# Revit family: Rotor XLR Series - IXLRADJ
name_source: partatom
category: Acessórios do tubo
units: mm (PartAtom-declared; Revit-internal decimal feet)

## family parameters
Com base no plano de trabalho = Não
Compartilhado = Não
Corte com vazios quando carregada = Não
Cota do conector redondo = Utilizar diâmetro
Número OmniClass = 23.60.30.11.14
Sempre na vertical = Sim
Tipo de parte = Normal
Título OmniClass = Pipework Fittings

## types (9) — shared parameters
Black Plastic = Black Plastic
Blue = Blue Plastic
Cobre = Cobre
DD4 = 1 '
Descrição = IXLRADJ Rotor
Fabricante = Rain Bird
Gray Plastic = Gray Plastic
Modelo = IXLRADJ
RainBird: Code = IXLRADJ
RainBird: Description = IXLRADJ Rotor
RainBird: Product Link = https://www.rainbird.com
Side inlet = Não
SupportProjetos: Level of Detail = LOD 300
SupportProjetos: Reviw = R00
TABLE 100 = TABLE 100psi
TABLE 110 = TABLE 110psi
TABLE 120 = TABLE 120psi
TABLE 30 = TABLE 30psi
TABLE 40 = TABLE 40psi
TABLE 50 = TABLE 50psi
TABLE 60 = TABLE 60psi
TABLE 70 = TABLE 70psi
TABLE 80 = TABLE 80psi
TABLE 90 = TABLE 90psi
URL = https://www.rainbird.com
Water = Water
zero-valued in all types: Body height, Conection, DD, DD1, DD10, DD11, DD12, DD13, DD3, DD5, DD7, Elevação padrão, H1, Pop up height, R1, R2, R3, R4, R5, RN, RT

## per-type parameters (varying)
| type | Angle | Instance |
| Nozzle 0.47 | 25.00° | 1 ' |
| Nozzle 0.55 | 25.00° | 2 ' |
| Nozzle 0.63 | 25.00° | 3 ' |
| Nozzle 0.71 | 25.00° | 4 ' |
| Nozzle 0.79 | 25.00° | 5 ' |
| Nozzle 0.87 | 25.00° | 6 ' |
| Nozzle 0.94 | 25.00° | 7 ' |
| Nozzle 1.02 | 25.00° | 8 ' |
| Nozzle 1.10 | 24.00° | 9 ' |
